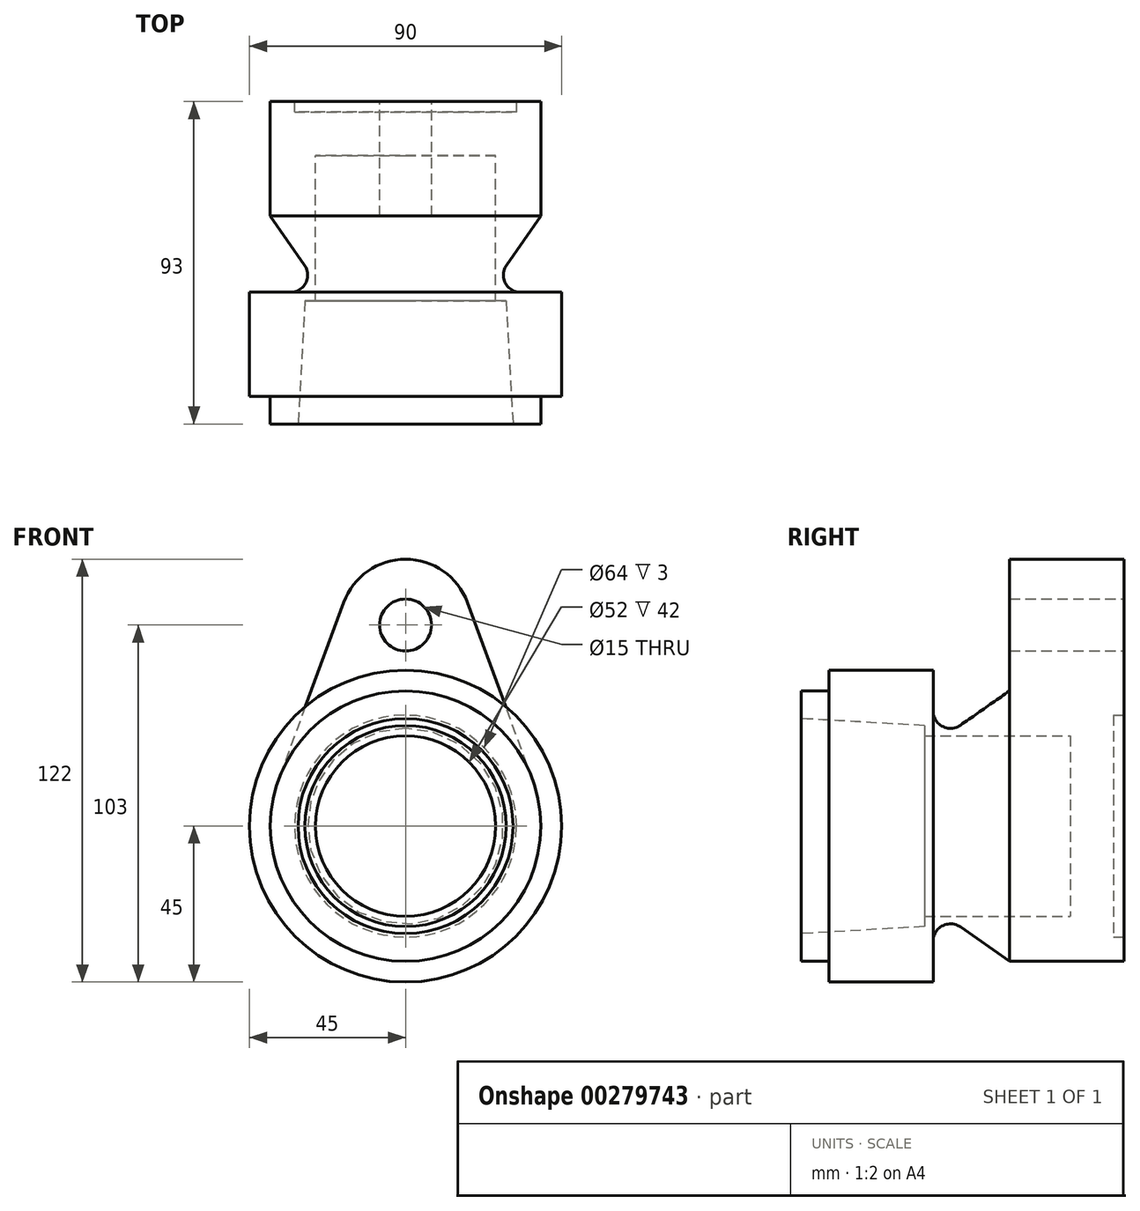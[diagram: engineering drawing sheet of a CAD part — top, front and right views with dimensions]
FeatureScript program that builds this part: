
annotation { "Feature Type Name" : "Feature", "Feature Type Description" : "" }
export const myFeature = defineFeature(function(context is Context, id is Id, definition is map)
    precondition{}
    {
        {
            var Q0;
            Q0=qCreatedBy(makeId("Right.planeOp"),FACE);
            var sketch = newSketch(context, id + "F0", { "sketchPlane" : qUnion([Q0])});
            skLineSegment(sketch, "E0", {"start": v(-12.04, 31) * mm, "end": v(-12.04, 39) * mm});
            skLineSegment(sketch, "E1", {"start": v(-12.04, 39) * mm, "end": v(-4.04, 39) * mm});
            skLineSegment(sketch, "E2", {"start": v(-4.04, 39) * mm, "end": v(-4.04, 39) * mm});
            skLineSegment(sketch, "E3", {"start": v(25.96, 39) * mm, "end": v(25.96, 33.2) * mm});
            skLineSegment(sketch, "E4", {"start": v(47.96, 39) * mm, "end": v(80.96, 39) * mm});
            skLineSegment(sketch, "E5", {"start": v(80.96, 39) * mm, "end": v(80.96, 32) * mm});
            skLineSegment(sketch, "E6", {"start": v(80.96, 32) * mm, "end": v(77.96, 32) * mm});
            skLineSegment(sketch, "E7", {"start": v(77.96, 32) * mm, "end": v(77.96, 0) * mm});
            skLineSegment(sketch, "E8", {"start": v(77.96, 0) * mm, "end": v(65.45, 0) * mm});
            skLineSegment(sketch, "E9", {"start": v(65.45, 0) * mm, "end": v(65.45, 26) * mm});
            skLineSegment(sketch, "E10", {"start": v(65.45, 26) * mm, "end": v(23.45, 26) * mm});
            skLineSegment(sketch, "E11", {"start": v(23.45, 26) * mm, "end": v(23.45, 29) * mm});
            skLineSegment(sketch, "E12", {"start": v(-4.04, 45) * mm, "end": v(25.96, 45) * mm});
            skLineSegment(sketch, "E13", {"start": v(-4.04, 39) * mm, "end": v(-4.04, 45) * mm});
            skLineSegment(sketch, "E14", {"start": v(25.96, 39) * mm, "end": v(25.96, 45) * mm});
            skLineSegment(sketch, "E15", {"start": v(-12.04, 31) * mm, "end": v(23.45, 29) * mm});
            skPoint(sketch, "E16.end.orphan", {"position": v(38.2, 32) * mm});
            skLineSegment(sketch, "E17", {"start": v(33.83, 29.1) * mm, "end": v(47.96, 39) * mm});
            skPoint(sketch, "E18.visualSharp", {"position": v(25.96, 23.6) * mm});
            skArc(sketch, "E18.filletArc", {"start": v(25.96, 33.2) * mm, "mid": v(28.65, 28.77) * mm, "end": v(33.83, 29.1) * mm});
            skSolve(sketch);
        }
        {
            var Q0;
            Q0=makeQuery(id+"F0.imprint","IMPRINT",FACE,{"disambiguationData":[TD([[makeQuery(id+"F0.imprint","IMPRINT",EDGE,{"derivedFrom":sQuery(id+"F0.wireOp",EDGE,"E0")}),-1.0]])]});
            var Q1;
            Q1=sQuery(id+"F0.wireOp",EDGE,"E8");
            revolve(context, id + "F1", {"entities" : qUnion([Q0]), "axis" : qUnion([Q1]), "revolveType" : RevolveType.FULL});
        }
        {
            var Q0;
            Q0=makeQuery(id+"F1.opRevolve","SWEPT_FACE",FACE,{"disambiguationData":[OSD([sQuery(id+"F0.wireOp",EDGE,"E5")])]});
            var sketch = newSketch(context, id + "F2", { "sketchPlane" : qUnion([Q0])});
            skLineSegment(sketch, "E19", {"start": v(0, 0) * mm, "end": v(0, 58) * mm, "construction": true});
            skLineSegment(sketch, "E20", {"start": v(-28.1, 58) * mm, "end": v(34.05, 58) * mm, "construction": true});
            skCircle(sketch, "E21", {"center": v(0, 58) * mm, "radius": 7.5 * mm});
            skArc(sketch, "E22", {"start": v(17.83, 64.55) * mm, "mid": v(0, 77) * mm, "end": v(-17.83, 64.55) * mm});
            skPoint(sketch, "E23.end.orphan", {"position": v(-40.5, 0) * mm});
            skPoint(sketch, "E24.orphan", {"position": v(40.5, 0) * mm});
            skLineSegment(sketch, "E25", {"start": v(-36.6, 13.45) * mm, "end": v(-17.83, 64.55) * mm});
            skLineSegment(sketch, "E26", {"start": v(-39, 0) * mm, "end": v(-82.19, 0) * mm, "construction": true});
            skPoint(sketch, "E27.orphan", {"position": v(36.6, 13.45) * mm});
            skPoint(sketch, "E28.start.orphan", {"position": v(19.66, 64.55) * mm});
            skLineSegment(sketch, "E29", {"start": v(17.83, 64.55) * mm, "end": v(36.6, 13.45) * mm});
            skArc(sketch, "E30", {"start": v(-36.6, 13.45) * mm, "mid": v(-38.4, 6.83) * mm, "end": v(-39, 0) * mm});
            skArc(sketch, "E31.trimOffspring", {"start": v(39, 0) * mm, "mid": v(38.4, 6.83) * mm, "end": v(36.6, 13.45) * mm});
            skArc(sketch, "E32.MirrorCS", {"start": v(17.83, -64.55) * mm, "mid": v(0, -77) * mm, "end": v(-17.83, -64.55) * mm});
            skLineSegment(sketch, "E33.MirrorCS", {"start": v(-36.6, -13.45) * mm, "end": v(-17.83, -64.55) * mm});
            skLineSegment(sketch, "E34.MirrorCS", {"start": v(17.83, -64.55) * mm, "end": v(36.6, -13.45) * mm});
            skArc(sketch, "E35.MirrorCS", {"start": v(39, 0) * mm, "mid": v(38.4, -6.83) * mm, "end": v(36.6, -13.45) * mm});
            skArc(sketch, "E36.MirrorCS", {"start": v(-36.6, -13.45) * mm, "mid": v(-38.4, -6.83) * mm, "end": v(-39, 0) * mm});
            skCircle(sketch, "E37.MirrorC", {"center": v(0, -58) * mm, "radius": 7.5 * mm});
            skSolve(sketch);
        }
        {
            var Q0;
            Q0=makeQuery(id+"F2.imprint","IMPRINT",FACE,{"disambiguationData":[TD([[makeQuery(id+"F2.imprint","IMPRINT",EDGE,{"derivedFrom":sQuery(id+"F2.wireOp",EDGE,"E21")}),-1.0]])]});
            var Q1;
            Q1=makeQuery(id+"F2.imprint","IMPRINT",FACE,{"disambiguationData":[TD([[makeQuery(id+"F2.imprint","IMPRINT",EDGE,{"derivedFrom":sQuery(id+"F2.wireOp",EDGE,"E32.MirrorCS")}),-1.0]])]});
            extrude(context, id + "F3", {"entities" : qUnion([Q0, Q1]), "operationType" : NewBodyOperationType.ADD, "oppositeDirection" : true, "depth" : 33 * mm});
        }
    });
